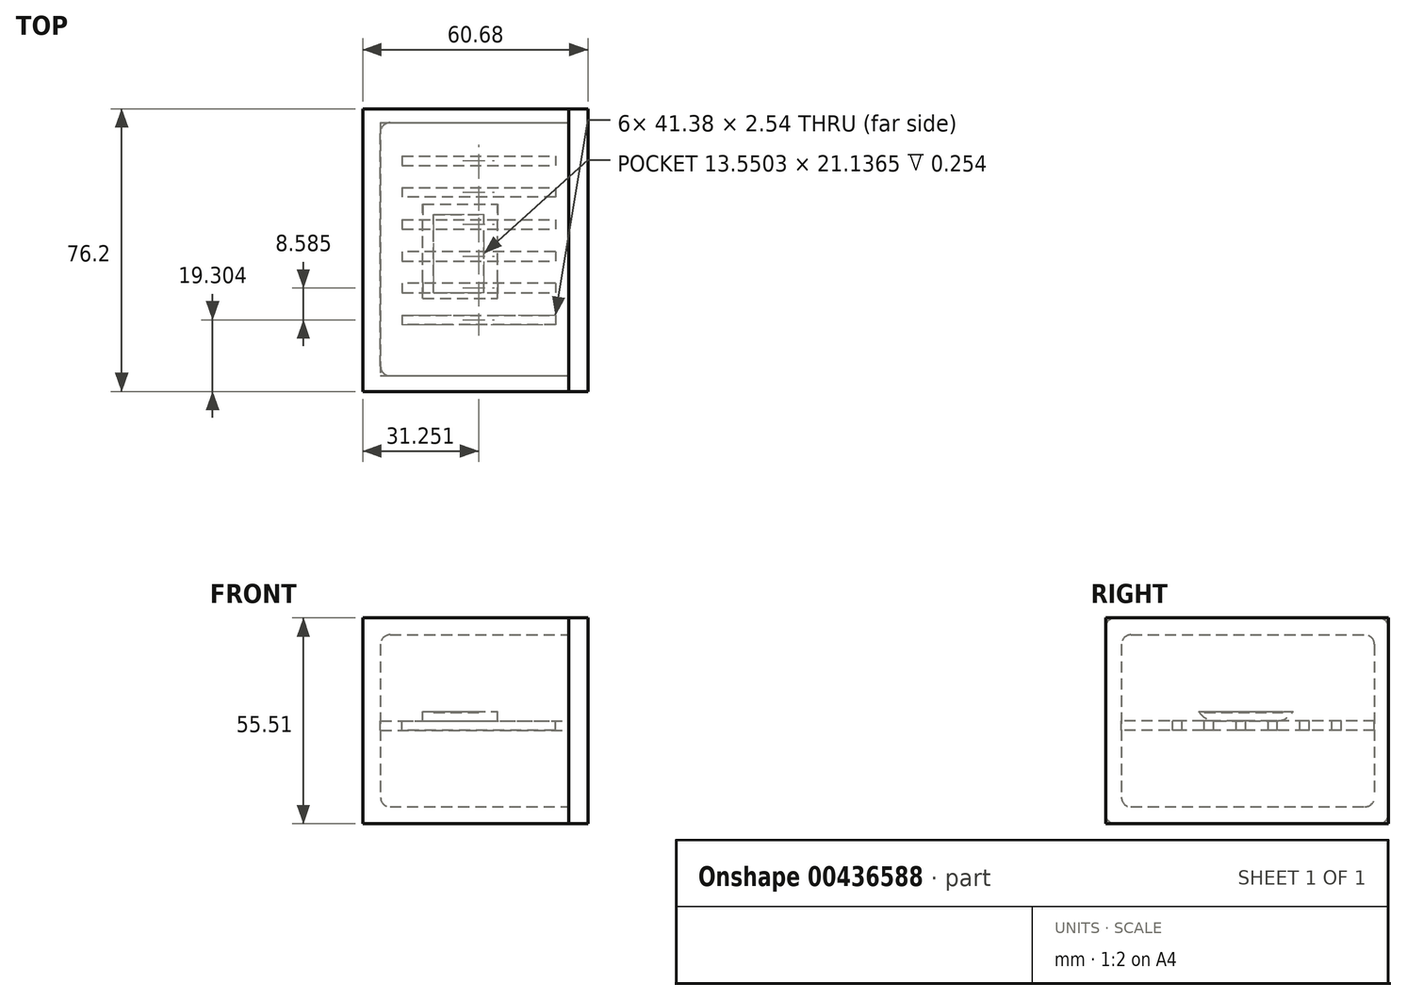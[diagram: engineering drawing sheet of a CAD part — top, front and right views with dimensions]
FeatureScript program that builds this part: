
annotation { "Feature Type Name" : "Feature", "Feature Type Description" : "" }
export const myFeature = defineFeature(function(context is Context, id is Id, definition is map)
    precondition{}
    {
        {
            var Q0;
            Q0=qCreatedBy(makeId("Front.planeOp"),FACE);
            var sketch = newSketch(context, id + "F0", { "sketchPlane" : qUnion([Q0])});
            skLineSegment(sketch, "E0.bottom", {"start": v(0, 0) * mm, "end": v(55.6, 0) * mm});
            skLineSegment(sketch, "E0.top", {"start": v(0, -55.5) * mm, "end": v(55.6, -55.5) * mm});
            skLineSegment(sketch, "E0.left", {"start": v(0, 0) * mm, "end": v(0, -55.5) * mm});
            skLineSegment(sketch, "E0.right", {"start": v(55.6, 0) * mm, "end": v(55.6, -55.5) * mm});
            skSolve(sketch);
        }
        {
            var Q0;
            Q0=makeQuery(id+"F0.imprint","IMPRINT",FACE,{"disambiguationData":[TD([[makeQuery(id+"F0.imprint","IMPRINT",EDGE,{"derivedFrom":sQuery(id+"F0.wireOp",EDGE,"E0.bottom")}),-1.0]])]});
            var Q1;
            Q1=sQuery(id+"F0.wireOp",EDGE,"E0.bottom");
            extrude(context, id + "F1", {"entities" : qUnion([Q0]), "surfaceEntities" : qUnion([Q1]), "depth" : 76.2 * mm});
        }
        {
            var Q0;
            Q0=makeQuery(id+"F1.opExtrude","SWEPT_FACE",FACE,{"disambiguationData":[OSD([sQuery(id+"F0.wireOp",EDGE,"E0.right")])]});
            var sketch = newSketch(context, id + "F2", { "sketchPlane" : qUnion([Q0])});
            skLineSegment(sketch, "E1.bottom", {"start": v(-71.95, -4.6) * mm, "end": v(-3.74, -4.6) * mm});
            skLineSegment(sketch, "E1.top", {"start": v(-71.95, -50.94) * mm, "end": v(-3.74, -50.94) * mm});
            skLineSegment(sketch, "E1.left", {"start": v(-71.95, -4.6) * mm, "end": v(-71.95, -50.94) * mm});
            skLineSegment(sketch, "E1.right", {"start": v(-3.74, -4.6) * mm, "end": v(-3.74, -50.94) * mm});
            skSolve(sketch);
        }
        {
            var Q0;
            Q0=makeQuery(id+"F2.imprint","IMPRINT",FACE,{"disambiguationData":[TD([[makeQuery(id+"F2.imprint","IMPRINT",EDGE,{"derivedFrom":sQuery(id+"F2.wireOp",EDGE,"E1.bottom")}),-1.0]])]});
            extrude(context, id + "F3", {"entities" : qUnion([Q0]), "operationType" : NewBodyOperationType.REMOVE, "endBound" : BoundingType.SYMMETRIC, "oppositeDirection" : true, "depth" : 101.6 * mm});
        }
        {
            var Q0;
            Q0=makeQuery(id+"F1.opExtrude","SWEPT_FACE",FACE,{"disambiguationData":[OSD([sQuery(id+"F0.wireOp",EDGE,"E0.right")])]});
            var sketch = newSketch(context, id + "F4", { "sketchPlane" : qUnion([Q0])});
            skLineSegment(sketch, "E2.bottom", {"start": v(-71.95, -27.77) * mm, "end": v(-3.74, -27.77) * mm});
            skLineSegment(sketch, "E3", {"start": v(-71.95, -27.77) * mm, "end": v(-71.95, -30.31) * mm});
            skLineSegment(sketch, "E4", {"start": v(-71.95, -30.31) * mm, "end": v(-3.74, -30.31) * mm});
            skLineSegment(sketch, "E5", {"start": v(-3.74, -30.31) * mm, "end": v(-3.74, -27.77) * mm});
            skSolve(sketch);
        }
        {
            var Q0;
            Q0=makeQuery(id+"F4.imprint","IMPRINT",FACE,{"disambiguationData":[TD([[makeQuery(id+"F4.imprint","IMPRINT",EDGE,{"derivedFrom":sQuery(id+"F4.wireOp",EDGE,"E2.bottom")}),-1.0]])]});
            extrude(context, id + "F5", {"entities" : qUnion([Q0]), "endBound" : BoundingType.UP_TO_NEXT, "oppositeDirection" : true, "depth" : 50.8 * mm});
        }
        {
            var Q0;
            Q0=makeQuery(id+"F5.opExtrude","SWEPT_FACE",FACE,{"disambiguationData":[OSD([sQuery(id+"F4.wireOp",EDGE,"E2.bottom")])]});
            var sketch = newSketch(context, id + "F6", { "sketchPlane" : qUnion([Q0])});
            skLineSegment(sketch, "E6.left", {"start": v(51.94, -12.7) * mm, "end": v(51.94, -15.24) * mm});
            skLineSegment(sketch, "E7", {"start": v(51.94, -21.29) * mm, "end": v(51.94, -23.83) * mm});
            skLineSegment(sketch, "E8", {"start": v(51.94, -29.87) * mm, "end": v(51.94, -32.41) * mm});
            skLineSegment(sketch, "E9", {"start": v(51.94, -38.46) * mm, "end": v(51.94, -41) * mm});
            skLineSegment(sketch, "E10", {"start": v(51.94, -47.04) * mm, "end": v(51.94, -49.58) * mm});
            skLineSegment(sketch, "E11", {"start": v(51.94, -55.63) * mm, "end": v(51.94, -58.17) * mm});
            skLineSegment(sketch, "E12", {"start": v(10.56, -12.7) * mm, "end": v(10.56, -15.24) * mm});
            skLineSegment(sketch, "E13", {"start": v(10.56, -21.29) * mm, "end": v(10.56, -23.83) * mm});
            skLineSegment(sketch, "E14", {"start": v(10.56, -29.87) * mm, "end": v(10.56, -32.41) * mm});
            skLineSegment(sketch, "E15", {"start": v(10.56, -47.04) * mm, "end": v(10.56, -49.58) * mm});
            skLineSegment(sketch, "E16", {"start": v(10.56, -55.63) * mm, "end": v(10.56, -58.17) * mm});
            skLineSegment(sketch, "E17", {"start": v(10.56, -38.46) * mm, "end": v(10.56, -41) * mm});
            skLineSegment(sketch, "E18", {"start": v(10.56, -12.7) * mm, "end": v(51.94, -12.7) * mm});
            skLineSegment(sketch, "E19", {"start": v(10.56, -15.24) * mm, "end": v(51.94, -15.24) * mm});
            skLineSegment(sketch, "E20", {"start": v(10.56, -21.29) * mm, "end": v(51.94, -21.29) * mm});
            skLineSegment(sketch, "E21", {"start": v(51.94, -23.83) * mm, "end": v(10.56, -23.83) * mm});
            skLineSegment(sketch, "E22", {"start": v(10.56, -29.87) * mm, "end": v(51.94, -29.87) * mm});
            skLineSegment(sketch, "E23", {"start": v(51.94, -38.46) * mm, "end": v(10.56, -38.46) * mm});
            skLineSegment(sketch, "E24", {"start": v(10.56, -41) * mm, "end": v(51.94, -41) * mm});
            skLineSegment(sketch, "E25", {"start": v(51.94, -47.04) * mm, "end": v(10.56, -47.04) * mm});
            skLineSegment(sketch, "E26", {"start": v(10.56, -49.58) * mm, "end": v(51.94, -49.58) * mm});
            skLineSegment(sketch, "E27", {"start": v(10.56, -55.63) * mm, "end": v(51.94, -55.63) * mm});
            skLineSegment(sketch, "E28", {"start": v(51.94, -58.17) * mm, "end": v(10.56, -58.17) * mm});
            skLineSegment(sketch, "E29", {"start": v(10.56, -32.41) * mm, "end": v(51.94, -32.41) * mm});
            skSolve(sketch);
        }
        {
            var Q0;
            Q0 = qSketchRegion(id + "F6", true);
            extrude(context, id + "F7", {"entities" : qUnion([Q0]), "operationType" : NewBodyOperationType.REMOVE, "endBound" : BoundingType.UP_TO_NEXT, "oppositeDirection" : true, "depth" : 25.4 * mm});
        }
        {
            var Q0;
            Q0=makeQuery(id+"F5.opExtrude","SWEPT_FACE",FACE,{"disambiguationData":[OSD([sQuery(id+"F4.wireOp",EDGE,"E2.bottom")])]});
            var sketch = newSketch(context, id + "F8", { "sketchPlane" : qUnion([Q0])});
            skLineSegment(sketch, "E30.bottom", {"start": v(16.2, -51.1) * mm, "end": v(36.41, -51.1) * mm});
            skLineSegment(sketch, "E30.top", {"start": v(16.2, -25.65) * mm, "end": v(36.41, -25.65) * mm});
            skLineSegment(sketch, "E30.left", {"start": v(16.2, -51.1) * mm, "end": v(16.2, -25.65) * mm});
            skLineSegment(sketch, "E30.right", {"start": v(36.41, -51.1) * mm, "end": v(36.41, -25.65) * mm});
            skSolve(sketch);
        }
        {
            var Q0;
            Q0 = qSketchRegion(id + "F8", true);
            extrude(context, id + "F9", {"entities" : qUnion([Q0]), "depth" : 2.54 * mm});
        }
        {
            var Q0;
            Q0=makeQuery(id+"F9.opExtrude","CAP_EDGE",EDGE,{"disambiguationData":[OSD([sQuery(id+"F8.wireOp",EDGE,"E30.top")])],"isStart":true});
            fillet(context, id + "F10", {"entities" : qUnion([Q0]), "radius" : 5.08 * mm, "tangentPropagation" : true, "allowEdgeOverflow" : false});
        }
        {
            var Q0;
            Q0=makeQuery(id+"F9.opExtrude","CAP_EDGE",EDGE,{"disambiguationData":[OSD([sQuery(id+"F8.wireOp",EDGE,"E30.bottom")])],"isStart":true});
            fillet(context, id + "F11", {"entities" : qUnion([Q0]), "radius" : 5.08 * mm, "tangentPropagation" : true, "allowEdgeOverflow" : false});
        }
        {
            var Q0;
            Q0=makeQuery(id+"F9.opExtrude","CAP_FACE",FACE,{"disambiguationData":[OSD([sQuery(id+"F8.wireOp",EDGE,"E30.bottom"),sQuery(id+"F8.wireOp",EDGE,"E30.top"),sQuery(id+"F8.wireOp",EDGE,"E30.left"),sQuery(id+"F8.wireOp",EDGE,"E30.right")])],"isStart":false});
            var sketch = newSketch(context, id + "F12", { "sketchPlane" : qUnion([Q0])});
            skLineSegment(sketch, "E31.bottom", {"start": v(19.12, -49.6) * mm, "end": v(32.67, -49.6) * mm});
            skLineSegment(sketch, "E31.top", {"start": v(19.12, -28.46) * mm, "end": v(32.67, -28.46) * mm});
            skLineSegment(sketch, "E31.left", {"start": v(19.12, -49.6) * mm, "end": v(19.12, -28.46) * mm});
            skLineSegment(sketch, "E31.right", {"start": v(32.67, -49.6) * mm, "end": v(32.67, -28.46) * mm});
            skSolve(sketch);
        }
        {
            var Q0;
            Q0 = qSketchRegion(id + "F12", true);
            extrude(context, id + "F13", {"entities" : qUnion([Q0]), "operationType" : NewBodyOperationType.REMOVE, "oppositeDirection" : true, "depth" : 0.25 * mm});
        }
        {
            var Q0;
            Q0=makeQuery(id+"F3.boolean.opBoolean","COPY",FACE,{"derivedFrom":makeQuery(id+"F3.opExtrude","SWEPT_FACE",FACE,{"disambiguationData":[OSD([sQuery(id+"F2.wireOp",EDGE,"E1.bottom")])]})});
            var sketch = newSketch(context, id + "F14", { "sketchPlane" : qUnion([Q0])});
            skCircle(sketch, "E32", {"center": v(32.63, 38.12) * mm, "radius": 1.82 * mm});
            skSolve(sketch);
        }
        {
            var Q0;
            Q0=makeQuery(id+"F1.opExtrude","CAP_EDGE",EDGE,{"disambiguationData":[OSD([sQuery(id+"F0.wireOp",EDGE,"E0.bottom")])],"isStart":true});
            fillet(context, id + "F15", {"entities" : qUnion([Q0]), "radius" : 2.54 * mm, "tangentPropagation" : true, "allowEdgeOverflow" : false});
        }
        {
            var Q0;
            Q0=makeQuery(id+"F1.opExtrude","CAP_EDGE",EDGE,{"disambiguationData":[OSD([sQuery(id+"F0.wireOp",EDGE,"E0.bottom")])],"isStart":false});
            fillet(context, id + "F16", {"entities" : qUnion([Q0]), "radius" : 2.54 * mm, "tangentPropagation" : true, "allowEdgeOverflow" : false});
        }
        {
            var Q0;
            Q0=sQuery(id+"F14.wireOp",EDGE,"E32");
            extrude(context, id + "F17", {"bodyType" : ToolBodyType.SURFACE, "surfaceEntities" : qUnion([Q0]), "depth" : 1.27 * mm});
        }
        {
            var Q0;
            Q0=makeQuery(id+"F3.boolean.opBoolean","COPY",EDGE,{"derivedFrom":makeQuery(id+"F3.opExtrude","SWEPT_EDGE",EDGE,{"disambiguationData":[OSD([sQuery(id+"F2.wireOp",EDGE,"E1.bottom"),sQuery(id+"F2.wireOp",EDGE,"E1.left")])]})});
            var Q1;
            Q1=makeQuery(id+"F3.boolean.opBoolean","COPY",EDGE,{"derivedFrom":makeQuery(id+"F3.opExtrude","CAP_EDGE",EDGE,{"disambiguationData":[OSD([sQuery(id+"F2.wireOp",EDGE,"E1.bottom")])],"isStart":false})});
            var Q2;
            Q2=makeQuery(id+"F3.boolean.opBoolean","COPY",EDGE,{"derivedFrom":makeQuery(id+"F3.opExtrude","SWEPT_EDGE",EDGE,{"disambiguationData":[OSD([sQuery(id+"F2.wireOp",EDGE,"E1.bottom"),sQuery(id+"F2.wireOp",EDGE,"E1.right")])]})});
            fillet(context, id + "F18", {"entities" : qUnion([Q0, Q1, Q2]), "radius" : 2.54 * mm, "tangentPropagation" : true, "allowEdgeOverflow" : false});
        }
        {
            var Q0;
            Q0=makeQuery(id+"F3.boolean.opBoolean","COPY",EDGE,{"derivedFrom":makeQuery(id+"F3.opExtrude","SWEPT_EDGE",EDGE,{"disambiguationData":[OSD([sQuery(id+"F2.wireOp",EDGE,"E1.top"),sQuery(id+"F2.wireOp",EDGE,"E1.left")])]})});
            var Q1;
            Q1=makeQuery(id+"F3.boolean.opBoolean","COPY",EDGE,{"derivedFrom":makeQuery(id+"F3.opExtrude","SWEPT_EDGE",EDGE,{"disambiguationData":[OSD([sQuery(id+"F2.wireOp",EDGE,"E1.top"),sQuery(id+"F2.wireOp",EDGE,"E1.right")])]})});
            fillet(context, id + "F19", {"entities" : qUnion([Q0, Q1]), "radius" : 2.54 * mm, "tangentPropagation" : true, "allowEdgeOverflow" : false});
        }
        {
            var Q0;
            Q0=makeQuery(id+"F3.boolean.opBoolean","COPY",EDGE,{"derivedFrom":makeQuery(id+"F3.opExtrude","CAP_EDGE",EDGE,{"disambiguationData":[OSD([sQuery(id+"F2.wireOp",EDGE,"E1.top")])],"isStart":false})});
            fillet(context, id + "F20", {"entities" : qUnion([Q0]), "radius" : 2.54 * mm, "tangentPropagation" : true, "allowEdgeOverflow" : false});
        }
        {
            var Q0;
            Q0=makeQuery(id+"F1.opExtrude","CAP_EDGE",EDGE,{"disambiguationData":[OSD([sQuery(id+"F0.wireOp",EDGE,"E0.top")])],"isStart":true});
            var Q1;
            Q1=makeQuery(id+"F1.opExtrude","CAP_EDGE",EDGE,{"disambiguationData":[OSD([sQuery(id+"F0.wireOp",EDGE,"E0.top")])],"isStart":false});
            fillet(context, id + "F21", {"entities" : qUnion([Q0, Q1]), "radius" : 2.54 * mm, "tangentPropagation" : true, "allowEdgeOverflow" : false});
        }
        {
            var Q0;
            Q0=makeQuery(id+"F1.opExtrude","SWEPT_FACE",FACE,{"disambiguationData":[OSD([sQuery(id+"F0.wireOp",EDGE,"E0.right")])]});
            var sketch = newSketch(context, id + "F22", { "sketchPlane" : qUnion([Q0])});
            skLineSegment(sketch, "E33.bottom", {"start": v(-76.2, 0) * mm, "end": v(0, 0) * mm});
            skLineSegment(sketch, "E33.top", {"start": v(-76.2, -55.5) * mm, "end": v(0, -55.5) * mm});
            skLineSegment(sketch, "E33.left", {"start": v(-76.2, 0) * mm, "end": v(-76.2, -55.5) * mm});
            skLineSegment(sketch, "E33.right", {"start": v(0, 0) * mm, "end": v(0, -55.5) * mm});
            skSolve(sketch);
        }
        {
            var Q0;
            Q0 = qSketchRegion(id + "F22", true);
            extrude(context, id + "F23", {"entities" : qUnion([Q0]), "depth" : 5.08 * mm});
        }
    });
